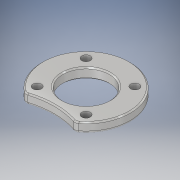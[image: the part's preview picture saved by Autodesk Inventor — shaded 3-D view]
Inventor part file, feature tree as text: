
AUTODESK INVENTOR PART (.ipt)
format: ipt  version: 2019.2 (Build 232265000, 265)  size: 195,072 bytes
history: native  units: mm
features: fillet x2, chamfer x2, extrude x1, sketch x1
ambient origin geometry x8: Origin, YZ Plane, XZ Plane, XY Plane, X Axis, Y Axis, Z Axis, Center Point
bodies: Solid1 (feature_tree)
feature tree (6):
  extrude  "Extrusion1"  Depth=3.75mm
  fillet  "Fillet1"  Radius=40.0mm
  fillet  "Fillet2"  [1 undecoded]
  chamfer  "Chamfer1"  Distance=20.0mm
  chamfer  "Chamfer2"  Distance=20.0mm
  sketch  "Sketch1"  dims[d0=18.5mm d2=3.4mm d4=40.0mm d6=360.0deg d8=45.0deg d10=20.0mm d11=20.0mm d12=4.0mm d13=0.0mm d14=2.0mm d15=1.0mm d24=0.5mm d25=2.0mm d26=45.0deg d27=1.0mm d30=7.5mm d31=3.75mm d32=0.5mm d33=2.0mm d34=45.0deg]
note: 1 required parameter value undecoded (feature->parameter linkage not recoverable at this tier; creation-order binding heuristic only, values carry confidence <= 0.55)
